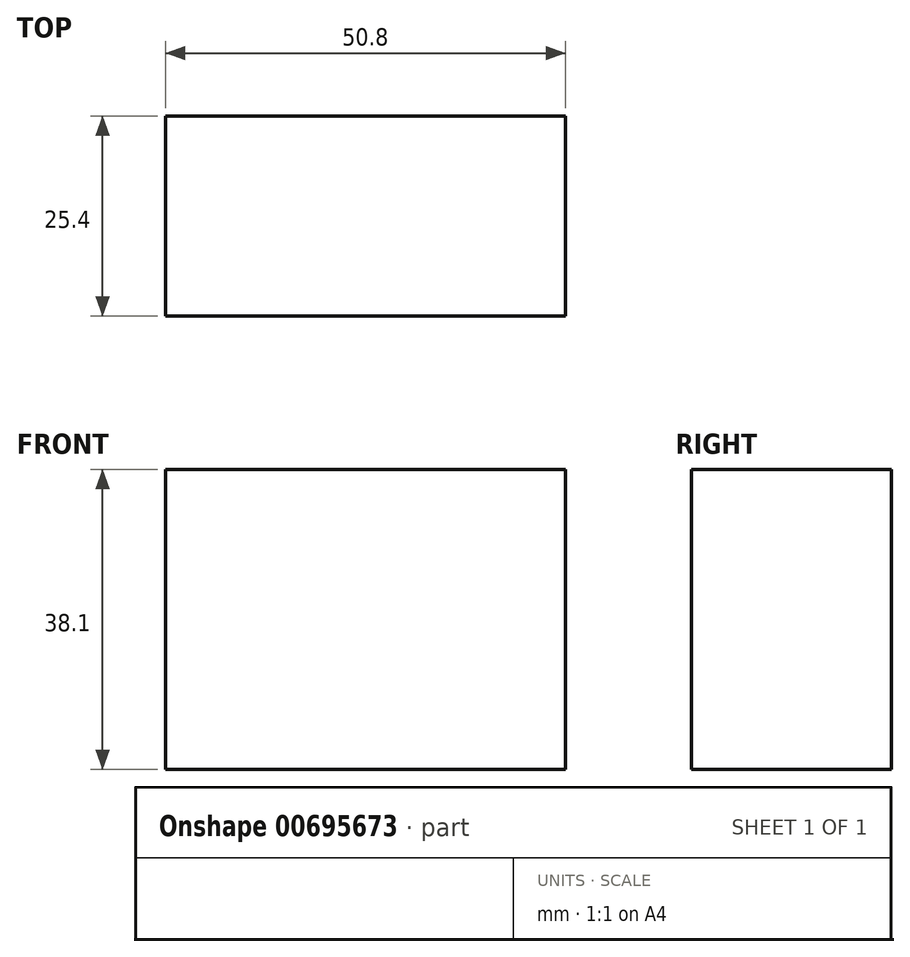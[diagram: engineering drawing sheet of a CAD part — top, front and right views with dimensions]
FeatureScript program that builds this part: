
annotation { "Feature Type Name" : "Feature", "Feature Type Description" : "" }
export const myFeature = defineFeature(function(context is Context, id is Id, definition is map)
    precondition{}
    {
        {
            var Q0;
            Q0=qCreatedBy(makeId("Front.planeOp"),FACE);
            var sketch = newSketch(context, id + "F0", { "sketchPlane" : qUnion([Q0])});
            skLineSegment(sketch, "E0.bottom", {"start": v(25.4, -19.05) * mm, "end": v(-25.4, -19.05) * mm});
            skLineSegment(sketch, "E0.top", {"start": v(25.4, 19.05) * mm, "end": v(-25.4, 19.05) * mm});
            skLineSegment(sketch, "E0.left", {"start": v(25.4, -19.05) * mm, "end": v(25.4, 19.05) * mm});
            skLineSegment(sketch, "E0.right", {"start": v(-25.4, -19.05) * mm, "end": v(-25.4, 19.05) * mm});
            skPoint(sketch, "E0.middle", {"position": v(0, 0) * mm});
            skSolve(sketch);
        }
        {
            var Q0;
            Q0=makeQuery(id+"F0.imprint","IMPRINT",FACE,{"disambiguationData":[TD([[makeQuery(id+"F0.imprint","IMPRINT",EDGE,{"derivedFrom":sQuery(id+"F0.wireOp",EDGE,"E0.bottom")}),-1.0]])]});
            extrude(context, id + "F1", {"entities" : qUnion([Q0]), "endBound" : BoundingType.SYMMETRIC, "depth" : 12.7 * mm, "offsetDistance" : 25.4 * mm});
        }
        {
            var Q0;
            Q0=makeQuery(id+"F1.opExtrude","CAP_FACE",FACE,{"disambiguationData":[OSD([sQuery(id+"F0.wireOp",EDGE,"E0.bottom"),sQuery(id+"F0.wireOp",EDGE,"E0.top"),sQuery(id+"F0.wireOp",EDGE,"E0.left"),sQuery(id+"F0.wireOp",EDGE,"E0.right")])],"isStart":true});
            var sketch = newSketch(context, id + "F2", { "sketchPlane" : qUnion([Q0])});
            skLineSegment(sketch, "E1.bottom", {"start": v(-25.4, -19.05) * mm, "end": v(25.4, -19.05) * mm});
            skLineSegment(sketch, "E1.top", {"start": v(-25.4, 19.05) * mm, "end": v(25.4, 19.05) * mm});
            skLineSegment(sketch, "E1.left", {"start": v(-25.4, -19.05) * mm, "end": v(-25.4, 19.05) * mm});
            skLineSegment(sketch, "E1.right", {"start": v(25.4, -19.05) * mm, "end": v(25.4, 19.05) * mm});
            skPoint(sketch, "E1.middle", {"position": v(0, 0) * mm});
            skSolve(sketch);
        }
        {
            var Q0;
            Q0 = qSketchRegion(id + "F2", true);
            extrude(context, id + "F3", {"entities" : qUnion([Q0]), "operationType" : NewBodyOperationType.ADD, "depth" : 12.7 * mm, "offsetDistance" : 25.4 * mm});
        }
    });
